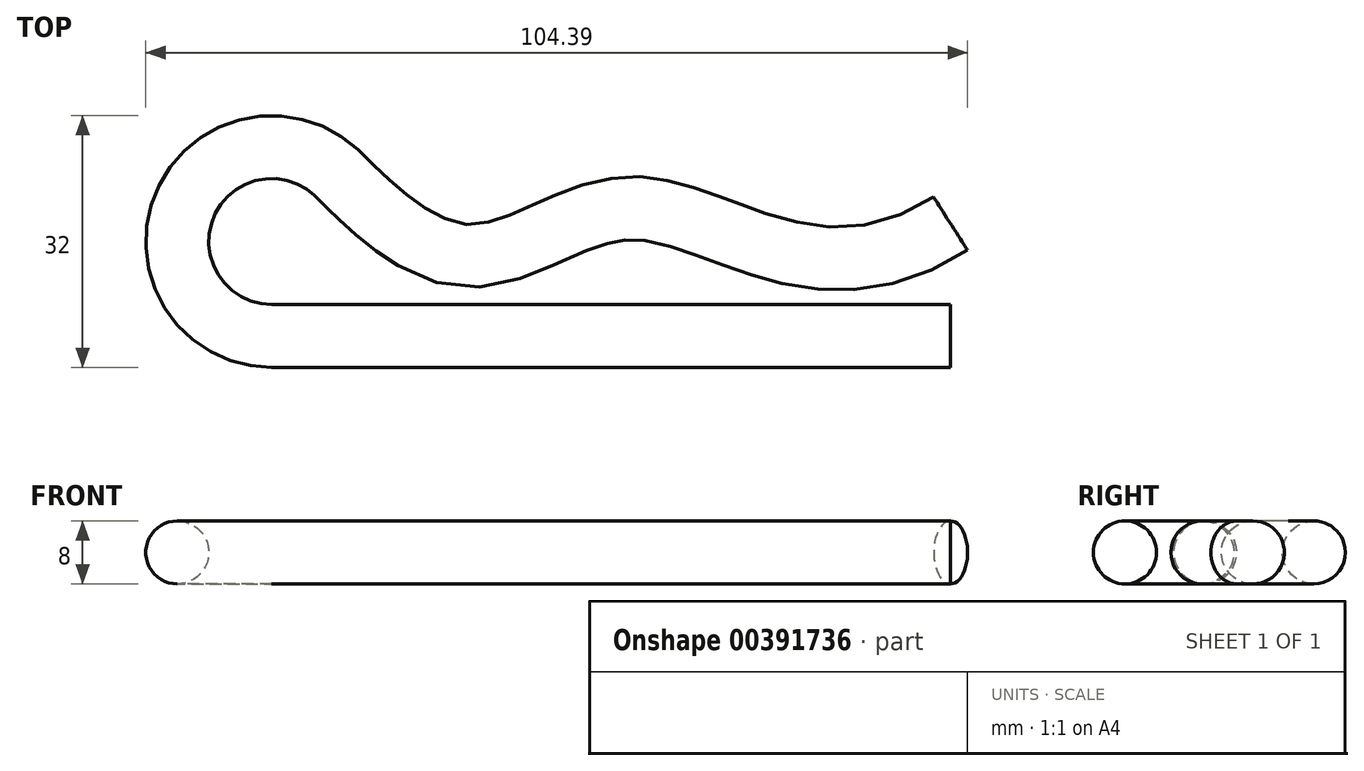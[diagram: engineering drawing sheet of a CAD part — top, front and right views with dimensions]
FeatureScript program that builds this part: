
annotation { "Feature Type Name" : "Feature", "Feature Type Description" : "" }
export const myFeature = defineFeature(function(context is Context, id is Id, definition is map)
    precondition{}
    {
        {
            var Q0;
            Q0=qCreatedBy(makeId("Top.planeOp"),FACE);
            var sketch = newSketch(context, id + "F0", { "sketchPlane" : qUnion([Q0])});
            skCircle(sketch, "E0", {"center": v(0, 0) * mm, "radius": 10 * mm, "construction": true});
            skLineSegment(sketch, "E1", {"start": v(40.17, 0) * mm, "end": v(-46.07, 0) * mm});
            skArc(sketch, "E2", {"start": v(-46.07, 0) * mm, "mid": v(-57.23, 16.41) * mm, "end": v(-37.86, 20.75) * mm});
            skFitSpline(sketch, "E3", {"points": [v(-37.86, 20.75) * mm, v(-22.66, 10.31) * mm, v(0, 16.25) * mm, v(40.17, 14.26) * mm], "startDerivative": vector(16.86, -15.81) * mm, "endDerivative": vector(125.72, 80.32) * mm});
            skSolve(sketch);
        }
        {
            var Q0;
            Q0=qCreatedBy(makeId("Right.planeOp"),FACE);
            var Q1;
            Q1=sQuery(id+"F0.wireOp",VERTEX,"E1.start");
            cPlane(context, id + "F1", {"entities" : qUnion([Q0, Q1]), "cplaneType" : CPlaneType.PLANE_POINT, "offset" : 25 * mm, "width" : 150 * mm, "height" : 150 * mm});
        }
        {
            var Q0;
            Q0=qCreatedBy(id+"F1.planeOp",FACE);
            var sketch = newSketch(context, id + "F2", { "sketchPlane" : qUnion([Q0])});
            skCircle(sketch, "E4", {"center": v(0, 0) * mm, "radius": 4 * mm});
            skSolve(sketch);
        }
        {
            var Q0;
            Q0=makeQuery(id+"F2.imprint","IMPRINT",FACE,{"disambiguationData":[TD([[makeQuery(id+"F2.imprint","IMPRINT",EDGE,{"derivedFrom":sQuery(id+"F2.wireOp",EDGE,"E4")}),1.0]])]});
            var Q1;
            Q1=sQuery(id+"F2.wireOp",EDGE,"E4");
            var Q2;
            Q2 = qConstructionFilter(qBodyType(qCreatedBy(id + "F0" ,EDGE), BodyType.WIRE), ConstructionObject.NO);
            sweep(context, id + "F3", {"profiles" : qUnion([Q0]), "surfaceProfiles" : qUnion([Q1]), "path" : qUnion([Q2])});
        }
    });
